# Revit family: Dachhalter Vlies
name_source: partatom
category: HLS-Bauteile
units: mm (PartAtom-declared; Revit-internal decimal feet)

## family parameters
Arbeitsebenenbasiert = Ja
Beim Laden mit Abzugskörper schneiden = Nein
Bemaßung runder Anschluss = Durchmesser verwenden
Beschriftungsausrichtung beibehalten = Nein
Gemeinsam genutzt = Ja
Immer vertikal = Nein
Klassifizierung = Keine
Raumberechnungspunkt = Nein
Teiletyp = Normal

## types (3) — shared parameters
Fabrikat = MEFA
Material = Kunststoff
Mengeneinheit = St
Stärke = 4 mm  [stored 0.0131234 ft]
Vorgabe-Ansicht = 1219 mm
vpe = 1

## per-type parameters (varying)
| type | Artikelnummer | Baustoffklasse | Breite | EAN | Farbe | Gewicht | Gewicht pro Bauteil | Kurztext1 | Kurztext2 | Länge | Materialname | max. Temperaturbeständigkeit | passend für |
| Dachhalter Vlies 600 | 08197618 |  | 600 mm | 4250928469434 | Weiß | 0,09 kg | 0,09 kg | Trennvlies 600 | 600 x 600 x 3,5 mm weiß | 600 mm |  |  | BIG FOOT® 400 und Dachhalter XL 80 |
| Dachhalter Vlies 305 | 08197603 |  | 345 mm  [stored 1.13189 ft] | 4250928455604 | Schwarz | 0,03 kg | 0,03 kg | Trennvlies BIG FOOT® 305 | 345 x 345 x 3,5 mm Polyester schwarz | 345 mm  [stored 1.13189 ft] | Polyester |  | BIG FOOT® 305 |
| Dachhalter Vlies 270 | 0819759701 | B1 | 270 mm  [stored 0.885827 ft] | 4250928449320 | Weiß | 0,03 kg | 0,03 kg | Trennvlies 45 | 270 x 270 x 3,5 mm Polyester weiß | 270 mm  [stored 0.885827 ft] | Polyester | 220 °C | Dachhalter 45 |

note: [stored X ft] marks values corroborated as IEEE doubles in the binary element streams (Revit-internal decimal feet)
